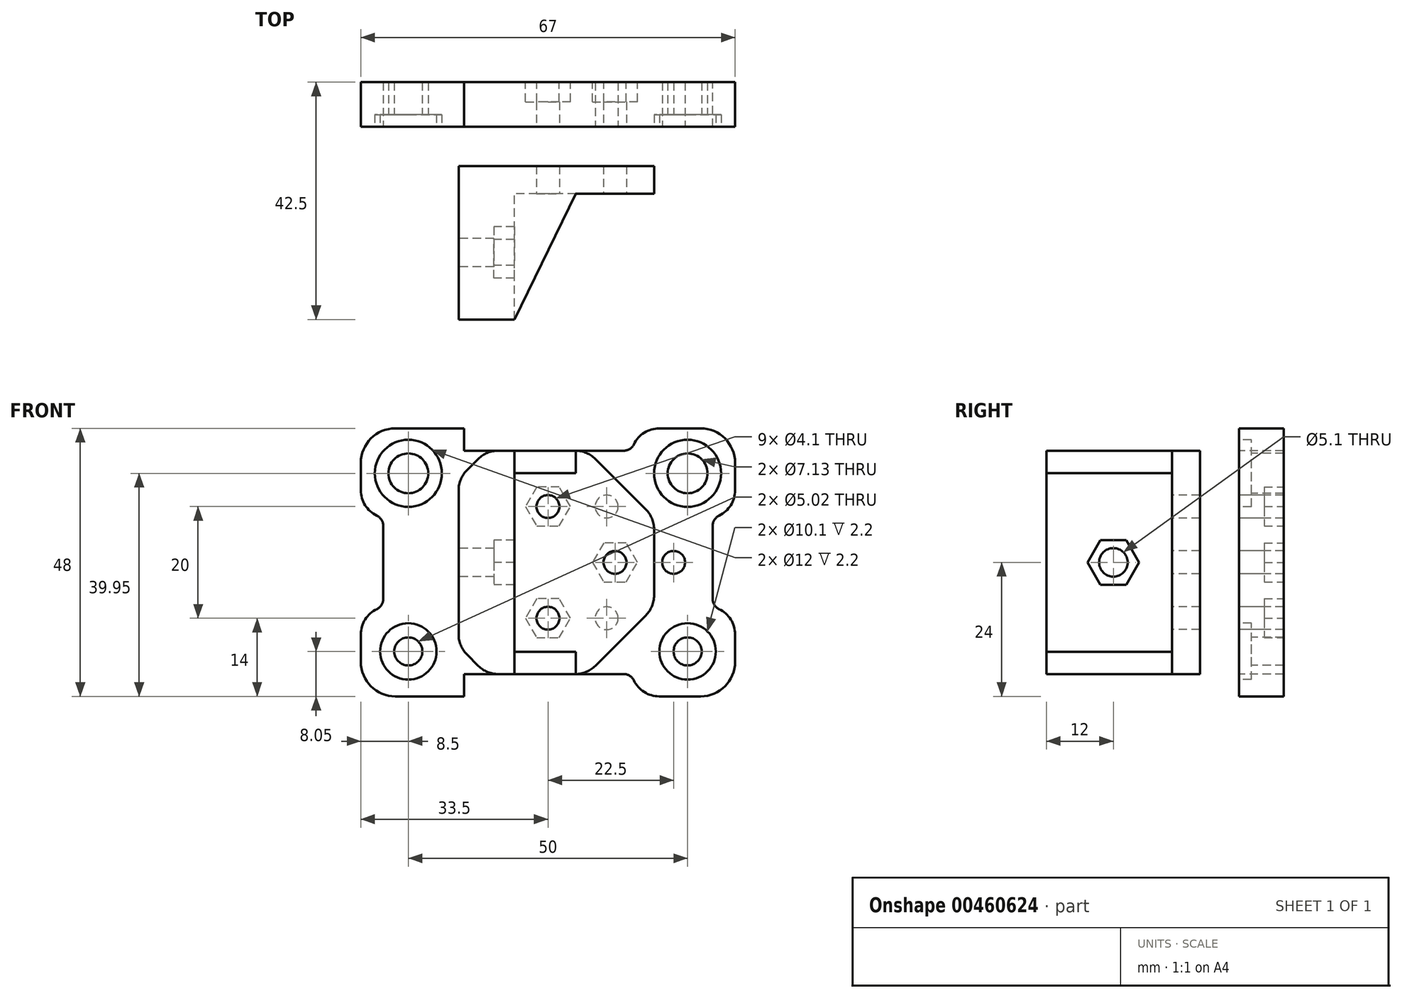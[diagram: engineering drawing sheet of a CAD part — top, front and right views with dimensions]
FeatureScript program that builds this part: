
annotation { "Feature Type Name" : "Feature", "Feature Type Description" : "" }
export const myFeature = defineFeature(function(context is Context, id is Id, definition is map)
    precondition{}
    {
        {
            var Q0;
            Q0=qCreatedBy(makeId("Front.planeOp"),FACE);
            var sketch = newSketch(context, id + "F0", { "sketchPlane" : qUnion([Q0])});
            skLineSegment(sketch, "E0.bottom", {"start": v(-33.5, 24) * mm, "end": v(33.5, 24) * mm});
            skLineSegment(sketch, "E0.top", {"start": v(-33.5, -24) * mm, "end": v(33.5, -24) * mm});
            skLineSegment(sketch, "E0.left", {"start": v(-33.5, 24) * mm, "end": v(-33.5, -24) * mm});
            skLineSegment(sketch, "E0.right", {"start": v(33.5, 24) * mm, "end": v(33.5, -24) * mm});
            skSolve(sketch);
        }
        {
            var Q0;
            Q0=makeQuery(id+"F0.imprint","IMPRINT",FACE,{"disambiguationData":[TD([[makeQuery(id+"F0.imprint","IMPRINT",EDGE,{"derivedFrom":sQuery(id+"F0.wireOp",EDGE,"E0.bottom")}),-1.0]])]});
            extrude(context, id + "F1", {"entities" : qUnion([Q0]), "depth" : 8 * mm, "offsetDistance" : 25 * mm});
        }
        {
            var Q0;
            Q0=makeQuery(id+"F1.opExtrude","SWEPT_EDGE",EDGE,{"disambiguationData":[OSD([sQuery(id+"F0.wireOp",EDGE,"E0.bottom"),sQuery(id+"F0.wireOp",EDGE,"E0.right")])]});
            var Q1;
            Q1=makeQuery(id+"F1.opExtrude","SWEPT_EDGE",EDGE,{"disambiguationData":[OSD([sQuery(id+"F0.wireOp",EDGE,"E0.bottom"),sQuery(id+"F0.wireOp",EDGE,"E0.left")])]});
            var Q2;
            Q2=makeQuery(id+"F1.opExtrude","SWEPT_EDGE",EDGE,{"disambiguationData":[OSD([sQuery(id+"F0.wireOp",EDGE,"E0.top"),sQuery(id+"F0.wireOp",EDGE,"E0.right")])]});
            var Q3;
            Q3=makeQuery(id+"F1.opExtrude","SWEPT_EDGE",EDGE,{"disambiguationData":[OSD([sQuery(id+"F0.wireOp",EDGE,"E0.top"),sQuery(id+"F0.wireOp",EDGE,"E0.left")])]});
            fillet(context, id + "F2", {"entities" : qUnion([Q0, Q1, Q2, Q3]), "radius" : 6.17 * mm, "tangentPropagation" : true, "allowEdgeOverflow" : false});
        }
        {
            var Q0;
            Q0=makeQuery(id+"F1.opExtrude","CAP_FACE",FACE,{"disambiguationData":[OSD([sQuery(id+"F0.wireOp",EDGE,"E0.bottom"),sQuery(id+"F0.wireOp",EDGE,"E0.top"),sQuery(id+"F0.wireOp",EDGE,"E0.left"),sQuery(id+"F0.wireOp",EDGE,"E0.right")])],"isStart":false});
            var sketch = newSketch(context, id + "F3", { "sketchPlane" : qUnion([Q0])});
            skCircle(sketch, "E1", {"center": v(25, 15.95) * mm, "radius": 3.56 * mm});
            skCircle(sketch, "E2", {"center": v(-25, 15.95) * mm, "radius": 3.56 * mm});
            skCircle(sketch, "E3", {"center": v(-25, -15.95) * mm, "radius": 2.5 * mm});
            skCircle(sketch, "E4", {"center": v(25, -15.95) * mm, "radius": 2.5 * mm});
            skCircle(sketch, "E5", {"center": v(12, 0) * mm, "radius": 2.05 * mm});
            skCircle(sketch, "E6", {"center": v(0, -10) * mm, "radius": 2.05 * mm});
            skCircle(sketch, "E7", {"center": v(0, 10) * mm, "radius": 2.05 * mm});
            skLineSegment(sketch, "E8.bottom", {"start": v(29.5, 8) * mm, "end": v(35, 8) * mm});
            skLineSegment(sketch, "E8.top", {"start": v(29.5, -8) * mm, "end": v(35, -8) * mm});
            skLineSegment(sketch, "E8.left", {"start": v(29.5, 8) * mm, "end": v(29.5, -8) * mm});
            skLineSegment(sketch, "E8.right", {"start": v(35, 8) * mm, "end": v(35, -8) * mm});
            skLineSegment(sketch, "E9.bottom", {"start": v(-35, 8) * mm, "end": v(-29.5, 8) * mm});
            skLineSegment(sketch, "E9.top", {"start": v(-35, -8) * mm, "end": v(-29.5, -8) * mm});
            skLineSegment(sketch, "E9.left", {"start": v(-35, 8) * mm, "end": v(-35, -8) * mm});
            skLineSegment(sketch, "E9.right", {"start": v(-29.5, 8) * mm, "end": v(-29.5, -8) * mm});
            skLineSegment(sketch, "E10.bottom", {"start": v(-15, 20) * mm, "end": v(15, 20) * mm});
            skLineSegment(sketch, "E10.top", {"start": v(-15, 24) * mm, "end": v(15, 24) * mm});
            skLineSegment(sketch, "E10.left", {"start": v(-15, 20) * mm, "end": v(-15, 24) * mm});
            skLineSegment(sketch, "E10.right", {"start": v(15, 20) * mm, "end": v(15, 24) * mm});
            skLineSegment(sketch, "E11.bottom", {"start": v(-15, -24) * mm, "end": v(15, -24) * mm});
            skLineSegment(sketch, "E11.top", {"start": v(-15, -20) * mm, "end": v(15, -20) * mm});
            skLineSegment(sketch, "E11.left", {"start": v(-15, -24) * mm, "end": v(-15, -20) * mm});
            skLineSegment(sketch, "E11.right", {"start": v(15, -24) * mm, "end": v(15, -20) * mm});
            skSolve(sketch);
        }
        {
            var Q0;
            Q0 = qSketchRegion(id + "F3", true);
            extrude(context, id + "F4", {"entities" : qUnion([Q0]), "operationType" : NewBodyOperationType.REMOVE, "endBound" : BoundingType.THROUGH_ALL, "oppositeDirection" : true, "depth" : 25 * mm});
        }
        {
            var Q0;
            Q0=makeQuery(id+"F1.opExtrude","CAP_FACE",FACE,{"disambiguationData":[OSD([sQuery(id+"F0.wireOp",EDGE,"E0.bottom"),sQuery(id+"F0.wireOp",EDGE,"E0.top"),sQuery(id+"F0.wireOp",EDGE,"E0.left"),sQuery(id+"F0.wireOp",EDGE,"E0.right")])],"isStart":false});
            var sketch = newSketch(context, id + "F5", { "sketchPlane" : qUnion([Q0])});
            skCircle(sketch, "E12", {"center": v(-25, 15.95) * mm, "radius": 6 * mm});
            skCircle(sketch, "E13", {"center": v(25, 15.95) * mm, "radius": 6 * mm});
            skCircle(sketch, "E14", {"center": v(25, -15.95) * mm, "radius": 5.05 * mm});
            skCircle(sketch, "E15", {"center": v(-25, -15.95) * mm, "radius": 5.05 * mm});
            skSolve(sketch);
        }
        {
            var Q0;
            Q0 = qSketchRegion(id + "F5", true);
            extrude(context, id + "F6", {"entities" : qUnion([Q0]), "operationType" : NewBodyOperationType.REMOVE, "oppositeDirection" : true, "depth" : 2.2 * mm});
        }
        {
            var Q0;
            Q0=makeQuery(id+"F1.opExtrude","CAP_FACE",FACE,{"disambiguationData":[OSD([sQuery(id+"F0.wireOp",EDGE,"E0.bottom"),sQuery(id+"F0.wireOp",EDGE,"E0.top"),sQuery(id+"F0.wireOp",EDGE,"E0.left"),sQuery(id+"F0.wireOp",EDGE,"E0.right")])],"isStart":true});
            var sketch = newSketch(context, id + "F7", { "sketchPlane" : qUnion([Q0])});
            skCircle(sketch, "E16.cCircle", {"center": v(0, 10) * mm, "radius": 3.5 * mm, "construction": true});
            skLineSegment(sketch, "E16.0", {"start": v(2.02, 6.5) * mm, "end": v(-2.02, 6.5) * mm});
            skLineSegment(sketch, "E16.1", {"start": v(-2.02, 6.5) * mm, "end": v(-4.04, 10) * mm});
            skLineSegment(sketch, "E16.2", {"start": v(-4.04, 10) * mm, "end": v(-2.02, 13.5) * mm});
            skLineSegment(sketch, "E16.3", {"start": v(-2.02, 13.5) * mm, "end": v(2.02, 13.5) * mm});
            skLineSegment(sketch, "E16.4", {"start": v(2.02, 13.5) * mm, "end": v(4.04, 10) * mm});
            skLineSegment(sketch, "E16.5", {"start": v(4.04, 10) * mm, "end": v(2.02, 6.5) * mm});
            skPoint(sketch, "E16.0.midPoint", {"position": v(0, 6.5) * mm});
            skCircle(sketch, "E17.cCircle", {"center": v(0, -10) * mm, "radius": 3.5 * mm, "construction": true});
            skLineSegment(sketch, "E17.0", {"start": v(4.04, -10) * mm, "end": v(2.02, -13.5) * mm});
            skLineSegment(sketch, "E17.1", {"start": v(2.02, -13.5) * mm, "end": v(-2.02, -13.5) * mm});
            skLineSegment(sketch, "E17.2", {"start": v(-2.02, -13.5) * mm, "end": v(-4.04, -10) * mm});
            skLineSegment(sketch, "E17.3", {"start": v(-4.04, -10) * mm, "end": v(-2.02, -6.5) * mm});
            skLineSegment(sketch, "E17.4", {"start": v(-2.02, -6.5) * mm, "end": v(2.02, -6.5) * mm});
            skLineSegment(sketch, "E17.5", {"start": v(2.02, -6.5) * mm, "end": v(4.04, -10) * mm});
            skPoint(sketch, "E17.0.midPoint", {"position": v(3.03, -11.75) * mm});
            skCircle(sketch, "E18.cCircle", {"center": v(-12, 0) * mm, "radius": 3.5 * mm, "construction": true});
            skLineSegment(sketch, "E18.0", {"start": v(-9.98, -3.5) * mm, "end": v(-14.02, -3.5) * mm});
            skLineSegment(sketch, "E18.1", {"start": v(-14.02, -3.5) * mm, "end": v(-16.04, 0) * mm});
            skLineSegment(sketch, "E18.2", {"start": v(-16.04, 0) * mm, "end": v(-14.02, 3.5) * mm});
            skLineSegment(sketch, "E18.3", {"start": v(-14.02, 3.5) * mm, "end": v(-9.98, 3.5) * mm});
            skLineSegment(sketch, "E18.4", {"start": v(-9.98, 3.5) * mm, "end": v(-7.96, 0) * mm});
            skLineSegment(sketch, "E18.5", {"start": v(-7.96, 0) * mm, "end": v(-9.98, -3.5) * mm});
            skPoint(sketch, "E18.0.midPoint", {"position": v(-12, -3.5) * mm});
            skSolve(sketch);
        }
        {
            var Q0;
            Q0 = qSketchRegion(id + "F7", true);
            extrude(context, id + "F8", {"entities" : qUnion([Q0]), "operationType" : NewBodyOperationType.REMOVE, "oppositeDirection" : true, "depth" : 3.5 * mm});
        }
        {
            var Q0;
            Q0=makeQuery(id+"F1.opExtrude","CAP_FACE",FACE,{"disambiguationData":[OSD([sQuery(id+"F0.wireOp",EDGE,"E0.bottom"),sQuery(id+"F0.wireOp",EDGE,"E0.top"),sQuery(id+"F0.wireOp",EDGE,"E0.left"),sQuery(id+"F0.wireOp",EDGE,"E0.right")])],"isStart":true});
            var sketch = newSketch(context, id + "F9", { "sketchPlane" : qUnion([Q0])});
            skLineSegment(sketch, "E19.bottom", {"start": v(29.5, 8) * mm, "end": v(33.5, 8) * mm});
            skLineSegment(sketch, "E19.top", {"start": v(29.5, -8) * mm, "end": v(33.5, -8) * mm});
            skLineSegment(sketch, "E19.left", {"start": v(29.5, 8) * mm, "end": v(29.5, -8) * mm});
            skLineSegment(sketch, "E19.right", {"start": v(33.5, 8) * mm, "end": v(33.5, -8) * mm});
            skLineSegment(sketch, "E20.bottom", {"start": v(-29.5, 8) * mm, "end": v(-33.5, 8) * mm});
            skLineSegment(sketch, "E20.top", {"start": v(-29.5, -8) * mm, "end": v(-33.5, -8) * mm});
            skLineSegment(sketch, "E20.left", {"start": v(-29.5, 8) * mm, "end": v(-29.5, -8) * mm});
            skLineSegment(sketch, "E20.right", {"start": v(-33.5, 8) * mm, "end": v(-33.5, -8) * mm});
            skSolve(sketch);
        }
        {
            var Q0;
            Q0 = qSketchRegion(id + "F9", true);
            extrude(context, id + "F10", {"entities" : qUnion([Q0]), "operationType" : NewBodyOperationType.REMOVE, "oppositeDirection" : true, "depth" : 2.5 * mm});
        }
        {
            var Q0;
            Q0=qCreatedBy(makeId("Front.planeOp"),FACE);
            cPlane(context, id + "F11", {"entities" : qUnion([Q0]), "cplaneType" : CPlaneType.OFFSET, "offset" : 15 * mm, "width" : 150 * mm, "height" : 150 * mm});
        }
        {
            var Q0;
            Q0=qCreatedBy(id+"F11.planeOp",FACE);
            var sketch = newSketch(context, id + "F12", { "sketchPlane" : qUnion([Q0])});
            skLineSegment(sketch, "E21", {"start": v(-5.5, -20) * mm, "end": v(-5.5, 20) * mm});
            skLineSegment(sketch, "E22", {"start": v(-5.5, 20) * mm, "end": v(29.5, 20) * mm});
            skLineSegment(sketch, "E23", {"start": v(29.5, 20) * mm, "end": v(29.5, -20) * mm});
            skLineSegment(sketch, "E24", {"start": v(29.5, -20) * mm, "end": v(-5.5, -20) * mm});
            skSolve(sketch);
        }
        {
            var Q0;
            Q0 = qSketchRegion(id + "F12", true);
            extrude(context, id + "F13", {"entities" : qUnion([Q0]), "depth" : 5 * mm});
        }
        {
            var Q0;
            Q0=makeQuery(id+"F13.opExtrude","CAP_FACE",FACE,{"disambiguationData":[OSD([sQuery(id+"F12.wireOp",EDGE,"E21"),sQuery(id+"F12.wireOp",EDGE,"E22"),sQuery(id+"F12.wireOp",EDGE,"E23"),sQuery(id+"F12.wireOp",EDGE,"E24")])],"isStart":false});
            var sketch = newSketch(context, id + "F14", { "sketchPlane" : qUnion([Q0])});
            skLineSegment(sketch, "E25.bottom", {"start": v(-5.5, -20) * mm, "end": v(4.5, -20) * mm});
            skLineSegment(sketch, "E25.top", {"start": v(-5.5, 20) * mm, "end": v(4.5, 20) * mm});
            skLineSegment(sketch, "E25.left", {"start": v(-5.5, -20) * mm, "end": v(-5.5, 20) * mm});
            skLineSegment(sketch, "E25.right", {"start": v(4.5, -20) * mm, "end": v(4.5, 20) * mm});
            skSolve(sketch);
        }
        {
            var Q0;
            Q0 = qSketchRegion(id + "F14", true);
            extrude(context, id + "F15", {"entities" : qUnion([Q0]), "operationType" : NewBodyOperationType.ADD, "depth" : 22.5 * mm, "offsetDistance" : 25 * mm});
        }
        {
            var Q0;
            Q0=makeQuery(id+"F13.opExtrude","SWEPT_EDGE",EDGE,{"disambiguationData":[OSD([sQuery(id+"F12.wireOp",EDGE,"E22"),sQuery(id+"F12.wireOp",EDGE,"E23")])]});
            var Q1;
            Q1=makeQuery(id+"F13.opExtrude","SWEPT_EDGE",EDGE,{"disambiguationData":[OSD([sQuery(id+"F12.wireOp",EDGE,"E23"),sQuery(id+"F12.wireOp",EDGE,"E24")])]});
            chamfer(context, id + "F16", {"entities" : qUnion([Q0, Q1]), "width" : 12 * mm, "tangentPropagation" : true});
        }
        {
            var Q0;
            {var subQ0=sQuery(id+"F12.wireOp",EDGE,"E22");Q0=makeQuery(id+"F16.opChamfer","BLEND_EDGE",EDGE,{"blendedFrom":[makeQuery(id+"F13.opExtrude","SWEPT_EDGE",EDGE,{"disambiguationData":[OSD([subQ0,sQuery(id+"F12.wireOp",EDGE,"E23")])]}),makeQuery(id+"F15.boolean.opBoolean","MERGE",FACE,{"derivedFrom":[makeQuery(id+"F13.opExtrude","SWEPT_FACE",FACE,{"disambiguationData":[OSD([subQ0])]}),makeQuery(id+"F15.opExtrude","SWEPT_FACE",FACE,{"disambiguationData":[OSD([sQuery(id+"F14.wireOp",EDGE,"E25.top")])]})]})],"blendedInto":[makeQuery(id+"F15.boolean.opBoolean","MERGE",FACE,{"derivedFrom":[makeQuery(id+"F13.opExtrude","SWEPT_FACE",FACE,{"disambiguationData":[OSD([subQ0])]}),makeQuery(id+"F15.opExtrude","SWEPT_FACE",FACE,{"disambiguationData":[OSD([sQuery(id+"F14.wireOp",EDGE,"E25.top")])]})]})]});}
            var Q1;
            {var subQ0=sQuery(id+"F12.wireOp",EDGE,"E23");Q1=makeQuery(id+"F16.opChamfer","BLEND_EDGE",EDGE,{"blendedFrom":[makeQuery(id+"F13.opExtrude","SWEPT_EDGE",EDGE,{"disambiguationData":[OSD([sQuery(id+"F12.wireOp",EDGE,"E22"),subQ0])]}),makeQuery(id+"F13.opExtrude","SWEPT_FACE",FACE,{"disambiguationData":[OSD([subQ0])]})],"blendedInto":[makeQuery(id+"F13.opExtrude","SWEPT_FACE",FACE,{"disambiguationData":[OSD([subQ0])]})]});}
            var Q2;
            {var subQ0=sQuery(id+"F12.wireOp",EDGE,"E23");Q2=makeQuery(id+"F16.opChamfer","BLEND_EDGE",EDGE,{"blendedFrom":[makeQuery(id+"F13.opExtrude","SWEPT_EDGE",EDGE,{"disambiguationData":[OSD([subQ0,sQuery(id+"F12.wireOp",EDGE,"E24")])]}),makeQuery(id+"F13.opExtrude","SWEPT_FACE",FACE,{"disambiguationData":[OSD([subQ0])]})],"blendedInto":[makeQuery(id+"F13.opExtrude","SWEPT_FACE",FACE,{"disambiguationData":[OSD([subQ0])]})]});}
            var Q3;
            {var subQ0=sQuery(id+"F12.wireOp",EDGE,"E24");Q3=makeQuery(id+"F16.opChamfer","BLEND_EDGE",EDGE,{"blendedFrom":[makeQuery(id+"F13.opExtrude","SWEPT_EDGE",EDGE,{"disambiguationData":[OSD([sQuery(id+"F12.wireOp",EDGE,"E23"),subQ0])]}),makeQuery(id+"F15.boolean.opBoolean","MERGE",FACE,{"derivedFrom":[makeQuery(id+"F13.opExtrude","SWEPT_FACE",FACE,{"disambiguationData":[OSD([subQ0])]}),makeQuery(id+"F15.opExtrude","SWEPT_FACE",FACE,{"disambiguationData":[OSD([sQuery(id+"F14.wireOp",EDGE,"E25.bottom")])]})]})],"blendedInto":[makeQuery(id+"F15.boolean.opBoolean","MERGE",FACE,{"derivedFrom":[makeQuery(id+"F13.opExtrude","SWEPT_FACE",FACE,{"disambiguationData":[OSD([subQ0])]}),makeQuery(id+"F15.opExtrude","SWEPT_FACE",FACE,{"disambiguationData":[OSD([sQuery(id+"F14.wireOp",EDGE,"E25.bottom")])]})]})]});}
            fillet(context, id + "F17", {"entities" : qUnion([Q0, Q1, Q2, Q3]), "radius" : 5 * mm, "tangentPropagation" : true, "allowEdgeOverflow" : false});
        }
        {
            var Q0;
            Q0=makeQuery(id+"F15.boolean.opBoolean","MERGE",EDGE,{"derivedFrom":[makeQuery(id+"F13.opExtrude","SWEPT_EDGE",EDGE,{"disambiguationData":[OSD([sQuery(id+"F12.wireOp",EDGE,"E21"),sQuery(id+"F12.wireOp",EDGE,"E22")])]}),makeQuery(id+"F15.opExtrude","SWEPT_EDGE",EDGE,{"disambiguationData":[OSD([sQuery(id+"F14.wireOp",EDGE,"E25.top"),sQuery(id+"F14.wireOp",EDGE,"E25.left")])]})]});
            var Q1;
            Q1=makeQuery(id+"F15.boolean.opBoolean","MERGE",EDGE,{"derivedFrom":[makeQuery(id+"F13.opExtrude","SWEPT_EDGE",EDGE,{"disambiguationData":[OSD([sQuery(id+"F12.wireOp",EDGE,"E21"),sQuery(id+"F12.wireOp",EDGE,"E24")])]}),makeQuery(id+"F15.opExtrude","SWEPT_EDGE",EDGE,{"disambiguationData":[OSD([sQuery(id+"F14.wireOp",EDGE,"E25.bottom"),sQuery(id+"F14.wireOp",EDGE,"E25.left")])]})]});
            chamfer(context, id + "F18", {"entities" : qUnion([Q0, Q1]), "width" : 5 * mm, "tangentPropagation" : true});
        }
        {
            var Q0;
            Q0=makeQuery(id+"F15.opExtrude","SWEPT_FACE",FACE,{"disambiguationData":[OSD([sQuery(id+"F14.wireOp",EDGE,"E25.right")])]});
            var sketch = newSketch(context, id + "F19", { "sketchPlane" : qUnion([Q0])});
            skLineSegment(sketch, "E26.bottom", {"start": v(-20, 20) * mm, "end": v(-42.5, 20) * mm});
            skLineSegment(sketch, "E26.top", {"start": v(-20, 16) * mm, "end": v(-42.5, 16) * mm});
            skLineSegment(sketch, "E26.left", {"start": v(-20, 20) * mm, "end": v(-20, 16) * mm});
            skLineSegment(sketch, "E26.right", {"start": v(-42.5, 20) * mm, "end": v(-42.5, 16) * mm});
            skLineSegment(sketch, "E27.bottom", {"start": v(-42.5, -20) * mm, "end": v(-20, -20) * mm});
            skLineSegment(sketch, "E27.top", {"start": v(-42.5, -16) * mm, "end": v(-20, -16) * mm});
            skLineSegment(sketch, "E27.left", {"start": v(-42.5, -20) * mm, "end": v(-42.5, -16) * mm});
            skLineSegment(sketch, "E27.right", {"start": v(-20, -20) * mm, "end": v(-20, -16) * mm});
            skSolve(sketch);
        }
        {
            var Q0;
            Q0 = qSketchRegion(id + "F19", true);
            extrude(context, id + "F20", {"entities" : qUnion([Q0]), "operationType" : NewBodyOperationType.ADD, "depth" : 11 * mm});
        }
        {
            var Q0;
            Q0=makeQuery(id+"F15.boolean.opBoolean","MERGE",FACE,{"derivedFrom":[makeQuery(id+"F13.opExtrude","SWEPT_FACE",FACE,{"disambiguationData":[OSD([sQuery(id+"F12.wireOp",EDGE,"E21")])]}),makeQuery(id+"F15.opExtrude","SWEPT_FACE",FACE,{"disambiguationData":[OSD([sQuery(id+"F14.wireOp",EDGE,"E25.left")])]})]});
            var sketch = newSketch(context, id + "F21", { "sketchPlane" : qUnion([Q0])});
            skCircle(sketch, "E28", {"center": v(30.5, 0) * mm, "radius": 2.55 * mm});
            skSolve(sketch);
        }
        {
            var Q0;
            Q0 = qSketchRegion(id + "F21", true);
            extrude(context, id + "F22", {"entities" : qUnion([Q0]), "operationType" : NewBodyOperationType.REMOVE, "endBound" : BoundingType.THROUGH_ALL, "oppositeDirection" : true, "depth" : 25 * mm});
        }
        {
            var Q0;
            Q0=makeQuery(id+"F15.boolean.opBoolean","MERGE",FACE,{"derivedFrom":[makeQuery(id+"F13.opExtrude","SWEPT_FACE",FACE,{"disambiguationData":[OSD([sQuery(id+"F12.wireOp",EDGE,"E21")])]}),makeQuery(id+"F15.opExtrude","SWEPT_FACE",FACE,{"disambiguationData":[OSD([sQuery(id+"F14.wireOp",EDGE,"E25.left")])]})]});
            var sketch = newSketch(context, id + "F23", { "sketchPlane" : qUnion([Q0])});
            skCircle(sketch, "E29.cCircle", {"center": v(30.5, 0) * mm, "radius": 4 * mm, "construction": true});
            skLineSegment(sketch, "E29.0", {"start": v(35.12, 0) * mm, "end": v(32.8, -4) * mm});
            skLineSegment(sketch, "E29.1", {"start": v(32.8, -4) * mm, "end": v(28.2, -4) * mm});
            skLineSegment(sketch, "E29.2", {"start": v(28.2, -4) * mm, "end": v(25.88, 0) * mm});
            skLineSegment(sketch, "E29.3", {"start": v(25.88, 0) * mm, "end": v(28.2, 4) * mm});
            skLineSegment(sketch, "E29.4", {"start": v(28.2, 4) * mm, "end": v(32.8, 4) * mm});
            skLineSegment(sketch, "E29.5", {"start": v(32.8, 4) * mm, "end": v(35.12, 0) * mm});
            skPoint(sketch, "E29.0.midPoint", {"position": v(33.96, -2) * mm});
            skSolve(sketch);
        }
        {
            var Q0;
            Q0 = qSketchRegion(id + "F23", true);
            extrude(context, id + "F24", {"entities" : qUnion([Q0]), "operationType" : NewBodyOperationType.REMOVE, "oppositeDirection" : true, "depth" : 30 * mm, "hasSecondDirection" : true, "secondDirectionOppositeDirection" : true, "secondDirectionDepth" : 6.3 * mm});
        }
        {
            var Q0;
            {var subQ0=sQuery(id+"F14.wireOp",EDGE,"E25.top");var subQ1=sQuery(id+"F12.wireOp",EDGE,"E22");Q0=makeQuery(id+"F18.opChamfer","BLEND_EDGE",EDGE,{"blendedFrom":[makeQuery(id+"F15.boolean.opBoolean","MERGE",EDGE,{"derivedFrom":[makeQuery(id+"F13.opExtrude","SWEPT_EDGE",EDGE,{"disambiguationData":[OSD([sQuery(id+"F12.wireOp",EDGE,"E21"),subQ1])]}),makeQuery(id+"F15.opExtrude","SWEPT_EDGE",EDGE,{"disambiguationData":[OSD([subQ0,sQuery(id+"F14.wireOp",EDGE,"E25.left")])]})]}),makeQuery(id+"F15.boolean.opBoolean","MERGE",FACE,{"derivedFrom":[makeQuery(id+"F13.opExtrude","SWEPT_FACE",FACE,{"disambiguationData":[OSD([subQ1])]}),makeQuery(id+"F15.opExtrude","SWEPT_FACE",FACE,{"disambiguationData":[OSD([subQ0])]})]})],"blendedInto":[makeQuery(id+"F15.boolean.opBoolean","MERGE",FACE,{"derivedFrom":[makeQuery(id+"F13.opExtrude","SWEPT_FACE",FACE,{"disambiguationData":[OSD([subQ1])]}),makeQuery(id+"F15.opExtrude","SWEPT_FACE",FACE,{"disambiguationData":[OSD([subQ0])]})]})]});}
            var Q1;
            {var subQ0=sQuery(id+"F14.wireOp",EDGE,"E25.bottom");var subQ1=sQuery(id+"F12.wireOp",EDGE,"E24");Q1=makeQuery(id+"F18.opChamfer","BLEND_EDGE",EDGE,{"blendedFrom":[makeQuery(id+"F15.boolean.opBoolean","MERGE",EDGE,{"derivedFrom":[makeQuery(id+"F13.opExtrude","SWEPT_EDGE",EDGE,{"disambiguationData":[OSD([sQuery(id+"F12.wireOp",EDGE,"E21"),subQ1])]}),makeQuery(id+"F15.opExtrude","SWEPT_EDGE",EDGE,{"disambiguationData":[OSD([subQ0,sQuery(id+"F14.wireOp",EDGE,"E25.left")])]})]}),makeQuery(id+"F15.boolean.opBoolean","MERGE",FACE,{"derivedFrom":[makeQuery(id+"F13.opExtrude","SWEPT_FACE",FACE,{"disambiguationData":[OSD([subQ1])]}),makeQuery(id+"F15.opExtrude","SWEPT_FACE",FACE,{"disambiguationData":[OSD([subQ0])]})]})],"blendedInto":[makeQuery(id+"F15.boolean.opBoolean","MERGE",FACE,{"derivedFrom":[makeQuery(id+"F13.opExtrude","SWEPT_FACE",FACE,{"disambiguationData":[OSD([subQ1])]}),makeQuery(id+"F15.opExtrude","SWEPT_FACE",FACE,{"disambiguationData":[OSD([subQ0])]})]})]});}
            var Q2;
            {var subQ0=sQuery(id+"F14.wireOp",EDGE,"E25.left");var subQ1=sQuery(id+"F12.wireOp",EDGE,"E21");Q2=makeQuery(id+"F18.opChamfer","BLEND_EDGE",EDGE,{"blendedFrom":[makeQuery(id+"F15.boolean.opBoolean","MERGE",EDGE,{"derivedFrom":[makeQuery(id+"F13.opExtrude","SWEPT_EDGE",EDGE,{"disambiguationData":[OSD([subQ1,sQuery(id+"F12.wireOp",EDGE,"E24")])]}),makeQuery(id+"F15.opExtrude","SWEPT_EDGE",EDGE,{"disambiguationData":[OSD([sQuery(id+"F14.wireOp",EDGE,"E25.bottom"),subQ0])]})]}),makeQuery(id+"F15.boolean.opBoolean","MERGE",FACE,{"derivedFrom":[makeQuery(id+"F13.opExtrude","SWEPT_FACE",FACE,{"disambiguationData":[OSD([subQ1])]}),makeQuery(id+"F15.opExtrude","SWEPT_FACE",FACE,{"disambiguationData":[OSD([subQ0])]})]})],"blendedInto":[makeQuery(id+"F15.boolean.opBoolean","MERGE",FACE,{"derivedFrom":[makeQuery(id+"F13.opExtrude","SWEPT_FACE",FACE,{"disambiguationData":[OSD([subQ1])]}),makeQuery(id+"F15.opExtrude","SWEPT_FACE",FACE,{"disambiguationData":[OSD([subQ0])]})]})]});}
            var Q3;
            {var subQ0=sQuery(id+"F14.wireOp",EDGE,"E25.left");var subQ1=sQuery(id+"F12.wireOp",EDGE,"E21");Q3=makeQuery(id+"F18.opChamfer","BLEND_EDGE",EDGE,{"blendedFrom":[makeQuery(id+"F15.boolean.opBoolean","MERGE",EDGE,{"derivedFrom":[makeQuery(id+"F13.opExtrude","SWEPT_EDGE",EDGE,{"disambiguationData":[OSD([subQ1,sQuery(id+"F12.wireOp",EDGE,"E22")])]}),makeQuery(id+"F15.opExtrude","SWEPT_EDGE",EDGE,{"disambiguationData":[OSD([sQuery(id+"F14.wireOp",EDGE,"E25.top"),subQ0])]})]}),makeQuery(id+"F15.boolean.opBoolean","MERGE",FACE,{"derivedFrom":[makeQuery(id+"F13.opExtrude","SWEPT_FACE",FACE,{"disambiguationData":[OSD([subQ1])]}),makeQuery(id+"F15.opExtrude","SWEPT_FACE",FACE,{"disambiguationData":[OSD([subQ0])]})]})],"blendedInto":[makeQuery(id+"F15.boolean.opBoolean","MERGE",FACE,{"derivedFrom":[makeQuery(id+"F13.opExtrude","SWEPT_FACE",FACE,{"disambiguationData":[OSD([subQ1])]}),makeQuery(id+"F15.opExtrude","SWEPT_FACE",FACE,{"disambiguationData":[OSD([subQ0])]})]})]});}
            fillet(context, id + "F25", {"entities" : qUnion([Q0, Q1, Q2, Q3]), "radius" : 5 * mm, "tangentPropagation" : true, "allowEdgeOverflow" : false});
        }
        {
            var Q0;
            Q0=makeQuery(id+"F4.boolean.opBoolean","INTERSECT",EDGE,{"derivedFrom":[makeQuery(id+"F1.opExtrude","SWEPT_FACE",FACE,{"disambiguationData":[OSD([sQuery(id+"F0.wireOp",EDGE,"E0.right")])]}),makeQuery(id+"F4.opExtrude","SWEPT_FACE",FACE,{"disambiguationData":[OSD([sQuery(id+"F3.wireOp",EDGE,"E8.bottom")])]})]});
            var Q1;
            Q1=makeQuery(id+"F4.boolean.opBoolean","INTERSECT",EDGE,{"derivedFrom":[makeQuery(id+"F1.opExtrude","SWEPT_FACE",FACE,{"disambiguationData":[OSD([sQuery(id+"F0.wireOp",EDGE,"E0.right")])]}),makeQuery(id+"F4.opExtrude","SWEPT_FACE",FACE,{"disambiguationData":[OSD([sQuery(id+"F3.wireOp",EDGE,"E8.top")])]})]});
            var Q2;
            Q2=makeQuery(id+"F4.boolean.opBoolean","INTERSECT",EDGE,{"derivedFrom":[makeQuery(id+"F1.opExtrude","SWEPT_FACE",FACE,{"disambiguationData":[OSD([sQuery(id+"F0.wireOp",EDGE,"E0.left")])]}),makeQuery(id+"F4.opExtrude","SWEPT_FACE",FACE,{"disambiguationData":[OSD([sQuery(id+"F3.wireOp",EDGE,"E9.top")])]})]});
            var Q3;
            Q3=makeQuery(id+"F4.boolean.opBoolean","INTERSECT",EDGE,{"derivedFrom":[makeQuery(id+"F1.opExtrude","SWEPT_FACE",FACE,{"disambiguationData":[OSD([sQuery(id+"F0.wireOp",EDGE,"E0.left")])]}),makeQuery(id+"F4.opExtrude","SWEPT_FACE",FACE,{"disambiguationData":[OSD([sQuery(id+"F3.wireOp",EDGE,"E9.bottom")])]})]});
            fillet(context, id + "F26", {"entities" : qUnion([Q0, Q1, Q2, Q3]), "radius" : 5 * mm, "tangentPropagation" : true, "allowEdgeOverflow" : false});
        }
        {
            var Q0;
            Q0=makeQuery(id+"F26.opFillet","BLEND_EDGE",EDGE,{"blendedFrom":[makeQuery(id+"F4.boolean.opBoolean","INTERSECT",EDGE,{"derivedFrom":[makeQuery(id+"F1.opExtrude","SWEPT_FACE",FACE,{"disambiguationData":[OSD([sQuery(id+"F0.wireOp",EDGE,"E0.left")])]}),makeQuery(id+"F4.opExtrude","SWEPT_FACE",FACE,{"disambiguationData":[OSD([sQuery(id+"F3.wireOp",EDGE,"E9.top")])]})]}),makeQuery(id+"F4.boolean.opBoolean","COPY",FACE,{"derivedFrom":makeQuery(id+"F4.opExtrude","SWEPT_FACE",FACE,{"disambiguationData":[OSD([sQuery(id+"F3.wireOp",EDGE,"E9.right")])]})})],"blendedInto":[makeQuery(id+"F4.boolean.opBoolean","COPY",FACE,{"derivedFrom":makeQuery(id+"F4.opExtrude","SWEPT_FACE",FACE,{"disambiguationData":[OSD([sQuery(id+"F3.wireOp",EDGE,"E9.right")])]})})]});
            var Q1;
            Q1=makeQuery(id+"F26.opFillet","BLEND_EDGE",EDGE,{"blendedFrom":[makeQuery(id+"F4.boolean.opBoolean","INTERSECT",EDGE,{"derivedFrom":[makeQuery(id+"F1.opExtrude","SWEPT_FACE",FACE,{"disambiguationData":[OSD([sQuery(id+"F0.wireOp",EDGE,"E0.left")])]}),makeQuery(id+"F4.opExtrude","SWEPT_FACE",FACE,{"disambiguationData":[OSD([sQuery(id+"F3.wireOp",EDGE,"E9.bottom")])]})]}),makeQuery(id+"F4.boolean.opBoolean","COPY",FACE,{"derivedFrom":makeQuery(id+"F4.opExtrude","SWEPT_FACE",FACE,{"disambiguationData":[OSD([sQuery(id+"F3.wireOp",EDGE,"E9.right")])]})})],"blendedInto":[makeQuery(id+"F4.boolean.opBoolean","COPY",FACE,{"derivedFrom":makeQuery(id+"F4.opExtrude","SWEPT_FACE",FACE,{"disambiguationData":[OSD([sQuery(id+"F3.wireOp",EDGE,"E9.right")])]})})]});
            var Q2;
            Q2=makeQuery(id+"F26.opFillet","BLEND_EDGE",EDGE,{"blendedFrom":[makeQuery(id+"F4.boolean.opBoolean","INTERSECT",EDGE,{"derivedFrom":[makeQuery(id+"F1.opExtrude","SWEPT_FACE",FACE,{"disambiguationData":[OSD([sQuery(id+"F0.wireOp",EDGE,"E0.right")])]}),makeQuery(id+"F4.opExtrude","SWEPT_FACE",FACE,{"disambiguationData":[OSD([sQuery(id+"F3.wireOp",EDGE,"E8.bottom")])]})]}),makeQuery(id+"F4.boolean.opBoolean","COPY",FACE,{"derivedFrom":makeQuery(id+"F4.opExtrude","SWEPT_FACE",FACE,{"disambiguationData":[OSD([sQuery(id+"F3.wireOp",EDGE,"E8.left")])]})})],"blendedInto":[makeQuery(id+"F4.boolean.opBoolean","COPY",FACE,{"derivedFrom":makeQuery(id+"F4.opExtrude","SWEPT_FACE",FACE,{"disambiguationData":[OSD([sQuery(id+"F3.wireOp",EDGE,"E8.left")])]})})]});
            var Q3;
            Q3=makeQuery(id+"F26.opFillet","BLEND_EDGE",EDGE,{"blendedFrom":[makeQuery(id+"F4.boolean.opBoolean","INTERSECT",EDGE,{"derivedFrom":[makeQuery(id+"F1.opExtrude","SWEPT_FACE",FACE,{"disambiguationData":[OSD([sQuery(id+"F0.wireOp",EDGE,"E0.right")])]}),makeQuery(id+"F4.opExtrude","SWEPT_FACE",FACE,{"disambiguationData":[OSD([sQuery(id+"F3.wireOp",EDGE,"E8.top")])]})]}),makeQuery(id+"F4.boolean.opBoolean","COPY",FACE,{"derivedFrom":makeQuery(id+"F4.opExtrude","SWEPT_FACE",FACE,{"disambiguationData":[OSD([sQuery(id+"F3.wireOp",EDGE,"E8.left")])]})})],"blendedInto":[makeQuery(id+"F4.boolean.opBoolean","COPY",FACE,{"derivedFrom":makeQuery(id+"F4.opExtrude","SWEPT_FACE",FACE,{"disambiguationData":[OSD([sQuery(id+"F3.wireOp",EDGE,"E8.left")])]})})]});
            fillet(context, id + "F27", {"entities" : qUnion([Q0, Q1, Q2, Q3]), "radius" : 2 * mm, "tangentPropagation" : true, "allowEdgeOverflow" : false});
        }
        {
            var Q0;
            Q0=makeQuery(id+"F4.boolean.opBoolean","COPY",EDGE,{"derivedFrom":makeQuery(id+"F4.opExtrude","SWEPT_EDGE",EDGE,{"disambiguationData":[OSD([sQuery(id+"F0.wireOp",EDGE,"E0.bottom"),sQuery(id+"F3.wireOp",EDGE,"E10.top"),sQuery(id+"F3.wireOp",EDGE,"E10.left")])]})});
            var Q1;
            Q1=makeQuery(id+"F4.boolean.opBoolean","COPY",EDGE,{"derivedFrom":makeQuery(id+"F4.opExtrude","SWEPT_EDGE",EDGE,{"disambiguationData":[OSD([sQuery(id+"F0.wireOp",EDGE,"E0.bottom"),sQuery(id+"F3.wireOp",EDGE,"E10.top"),sQuery(id+"F3.wireOp",EDGE,"E10.right")])]})});
            var Q2;
            Q2=makeQuery(id+"F4.boolean.opBoolean","COPY",EDGE,{"derivedFrom":makeQuery(id+"F4.opExtrude","SWEPT_EDGE",EDGE,{"disambiguationData":[OSD([sQuery(id+"F0.wireOp",EDGE,"E0.top"),sQuery(id+"F3.wireOp",EDGE,"E11.bottom"),sQuery(id+"F3.wireOp",EDGE,"E11.right")])]})});
            var Q3;
            Q3=makeQuery(id+"F4.boolean.opBoolean","COPY",EDGE,{"derivedFrom":makeQuery(id+"F4.opExtrude","SWEPT_EDGE",EDGE,{"disambiguationData":[OSD([sQuery(id+"F0.wireOp",EDGE,"E0.top"),sQuery(id+"F3.wireOp",EDGE,"E11.bottom"),sQuery(id+"F3.wireOp",EDGE,"E11.left")])]})});
            fillet(context, id + "F28", {"entities" : qUnion([Q0, Q1, Q2, Q3]), "radius" : 5 * mm, "tangentPropagation" : true, "allowEdgeOverflow" : false});
        }
        {
            var Q0;
            Q0=makeQuery(id+"F28.opFillet","BLEND_EDGE",EDGE,{"blendedFrom":[makeQuery(id+"F4.boolean.opBoolean","COPY",EDGE,{"derivedFrom":makeQuery(id+"F4.opExtrude","SWEPT_EDGE",EDGE,{"disambiguationData":[OSD([sQuery(id+"F0.wireOp",EDGE,"E0.bottom"),sQuery(id+"F3.wireOp",EDGE,"E10.top"),sQuery(id+"F3.wireOp",EDGE,"E10.left")])]})}),makeQuery(id+"F4.boolean.opBoolean","COPY",FACE,{"derivedFrom":makeQuery(id+"F4.opExtrude","SWEPT_FACE",FACE,{"disambiguationData":[OSD([sQuery(id+"F3.wireOp",EDGE,"E10.bottom")])]})})],"blendedInto":[makeQuery(id+"F4.boolean.opBoolean","COPY",FACE,{"derivedFrom":makeQuery(id+"F4.opExtrude","SWEPT_FACE",FACE,{"disambiguationData":[OSD([sQuery(id+"F3.wireOp",EDGE,"E10.bottom")])]})})]});
            var Q1;
            Q1=makeQuery(id+"F28.opFillet","BLEND_EDGE",EDGE,{"blendedFrom":[makeQuery(id+"F4.boolean.opBoolean","COPY",EDGE,{"derivedFrom":makeQuery(id+"F4.opExtrude","SWEPT_EDGE",EDGE,{"disambiguationData":[OSD([sQuery(id+"F0.wireOp",EDGE,"E0.bottom"),sQuery(id+"F3.wireOp",EDGE,"E10.top"),sQuery(id+"F3.wireOp",EDGE,"E10.right")])]})}),makeQuery(id+"F4.boolean.opBoolean","COPY",FACE,{"derivedFrom":makeQuery(id+"F4.opExtrude","SWEPT_FACE",FACE,{"disambiguationData":[OSD([sQuery(id+"F3.wireOp",EDGE,"E10.bottom")])]})})],"blendedInto":[makeQuery(id+"F4.boolean.opBoolean","COPY",FACE,{"derivedFrom":makeQuery(id+"F4.opExtrude","SWEPT_FACE",FACE,{"disambiguationData":[OSD([sQuery(id+"F3.wireOp",EDGE,"E10.bottom")])]})})]});
            var Q2;
            Q2=makeQuery(id+"F28.opFillet","BLEND_EDGE",EDGE,{"blendedFrom":[makeQuery(id+"F4.boolean.opBoolean","COPY",EDGE,{"derivedFrom":makeQuery(id+"F4.opExtrude","SWEPT_EDGE",EDGE,{"disambiguationData":[OSD([sQuery(id+"F0.wireOp",EDGE,"E0.top"),sQuery(id+"F3.wireOp",EDGE,"E11.bottom"),sQuery(id+"F3.wireOp",EDGE,"E11.right")])]})}),makeQuery(id+"F4.boolean.opBoolean","COPY",FACE,{"derivedFrom":makeQuery(id+"F4.opExtrude","SWEPT_FACE",FACE,{"disambiguationData":[OSD([sQuery(id+"F3.wireOp",EDGE,"E11.top")])]})})],"blendedInto":[makeQuery(id+"F4.boolean.opBoolean","COPY",FACE,{"derivedFrom":makeQuery(id+"F4.opExtrude","SWEPT_FACE",FACE,{"disambiguationData":[OSD([sQuery(id+"F3.wireOp",EDGE,"E11.top")])]})})]});
            var Q3;
            Q3=makeQuery(id+"F28.opFillet","BLEND_EDGE",EDGE,{"blendedFrom":[makeQuery(id+"F4.boolean.opBoolean","COPY",EDGE,{"derivedFrom":makeQuery(id+"F4.opExtrude","SWEPT_EDGE",EDGE,{"disambiguationData":[OSD([sQuery(id+"F0.wireOp",EDGE,"E0.top"),sQuery(id+"F3.wireOp",EDGE,"E11.bottom"),sQuery(id+"F3.wireOp",EDGE,"E11.left")])]})}),makeQuery(id+"F4.boolean.opBoolean","COPY",FACE,{"derivedFrom":makeQuery(id+"F4.opExtrude","SWEPT_FACE",FACE,{"disambiguationData":[OSD([sQuery(id+"F3.wireOp",EDGE,"E11.top")])]})})],"blendedInto":[makeQuery(id+"F4.boolean.opBoolean","COPY",FACE,{"derivedFrom":makeQuery(id+"F4.opExtrude","SWEPT_FACE",FACE,{"disambiguationData":[OSD([sQuery(id+"F3.wireOp",EDGE,"E11.top")])]})})]});
            fillet(context, id + "F29", {"entities" : qUnion([Q0, Q1, Q2, Q3]), "radius" : 2 * mm, "tangentPropagation" : true, "allowEdgeOverflow" : false});
        }
        {
            var Q0;
            Q0=makeQuery(id+"F13.opExtrude","CAP_FACE",FACE,{"disambiguationData":[OSD([sQuery(id+"F12.wireOp",EDGE,"E21"),sQuery(id+"F12.wireOp",EDGE,"E22"),sQuery(id+"F12.wireOp",EDGE,"E23"),sQuery(id+"F12.wireOp",EDGE,"E24")])],"isStart":false});
            var sketch = newSketch(context, id + "F30", { "sketchPlane" : qUnion([Q0])});
            skCircle(sketch, "E30", {"center": v(10.5, 10) * mm, "radius": 2.05 * mm});
            skCircle(sketch, "E31", {"center": v(10.5, -10) * mm, "radius": 2.05 * mm});
            skCircle(sketch, "E32", {"center": v(22.5, 0) * mm, "radius": 2.05 * mm});
            skSolve(sketch);
        }
        {
            var Q0;
            Q0 = qSketchRegion(id + "F30", true);
            extrude(context, id + "F31", {"entities" : qUnion([Q0]), "operationType" : NewBodyOperationType.REMOVE, "oppositeDirection" : true, "depth" : 25 * mm});
        }
        {
            var Q0;
            Q0=makeQuery(id+"F13.opExtrude","SWEPT_BODY",BODY,{"disambiguationData":[OSD([sQuery(id+"F12.wireOp",EDGE,"E21"),sQuery(id+"F12.wireOp",EDGE,"E22"),sQuery(id+"F12.wireOp",EDGE,"E23"),sQuery(id+"F12.wireOp",EDGE,"E24")])]});
            transform(context, id + "F32", {"entities" : qUnion([Q0]), "transformType" : TransformType.TRANSLATION_3D, "dx" : -10.5 * mm, "dy" : 0 * mm, "dz" : 0 * mm, "makeCopy" : false});
        }
        {
            var Q0;
            Q0=makeQuery(id+"F20.opExtrude","CAP_EDGE",EDGE,{"disambiguationData":[OSD([sQuery(id+"F19.wireOp",EDGE,"E27.left")])],"isStart":false});
            var Q1;
            Q1=makeQuery(id+"F20.opExtrude","CAP_EDGE",EDGE,{"disambiguationData":[OSD([sQuery(id+"F19.wireOp",EDGE,"E26.right")])],"isStart":false});
            chamfer(context, id + "F33", {"entities" : qUnion([Q0, Q1]), "chamferType" : ChamferType.TWO_OFFSETS, "width1" : 11 * mm, "oppositeDirection" : false, "width2" : 22.5 * mm, "tangentPropagation" : true});
        }
    });
